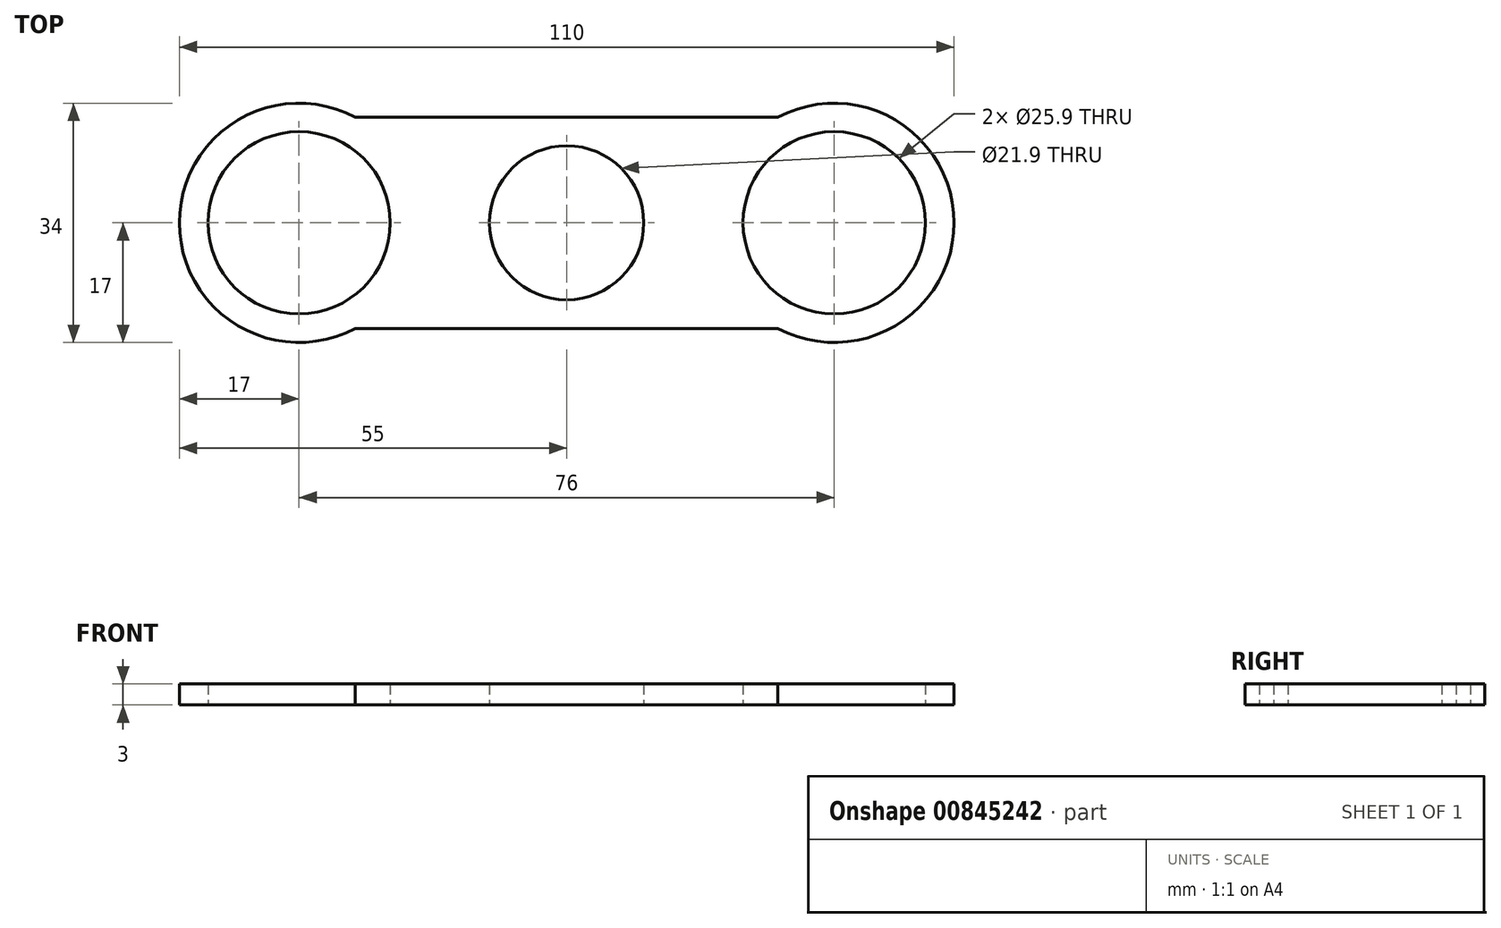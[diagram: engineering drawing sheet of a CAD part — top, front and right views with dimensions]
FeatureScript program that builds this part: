
annotation { "Feature Type Name" : "Feature", "Feature Type Description" : "" }
export const myFeature = defineFeature(function(context is Context, id is Id, definition is map)
    precondition{}
    {
        {
            var Q0;
            Q0=qCreatedBy(makeId("Top.planeOp"),FACE);
            var sketch = newSketch(context, id + "F0", { "sketchPlane" : qUnion([Q0])});
            skArc(sketch, "E0.1.3", {"start": v(-30, 15) * mm, "mid": v(-55, 0) * mm, "end": v(-30, -15) * mm});
            skPoint(sketch, "E0.center", {"position": v(0, 0) * mm});
            skLineSegment(sketch, "E1", {"start": v(-30, -15) * mm, "end": v(0, -15) * mm});
            skCircle(sketch, "E2", {"center": v(-38, 0) * mm, "radius": 12.95 * mm});
            skArc(sketch, "E3.MirrorCS", {"start": v(30, 15) * mm, "mid": v(55, 0) * mm, "end": v(30, -15) * mm});
            skCircle(sketch, "E4.MirrorC", {"center": v(38, 0) * mm, "radius": 12.95 * mm});
            skLineSegment(sketch, "E5.MirrorCS", {"start": v(30, -15) * mm, "end": v(0, -15) * mm});
            skCircle(sketch, "E6", {"center": v(0, 0) * mm, "radius": 10.95 * mm});
            skLineSegment(sketch, "E7", {"start": v(-30, 15) * mm, "end": v(30, 15) * mm});
            skSolve(sketch);
        }
        {
            var Q0;
            Q0=qSketchRegion(id+"F0",true);
            extrude(context, id + "F1", {"entities" : qUnion([Q0]), "depth" : 3 * mm, "offsetDistance" : 25 * mm});
        }
    });
